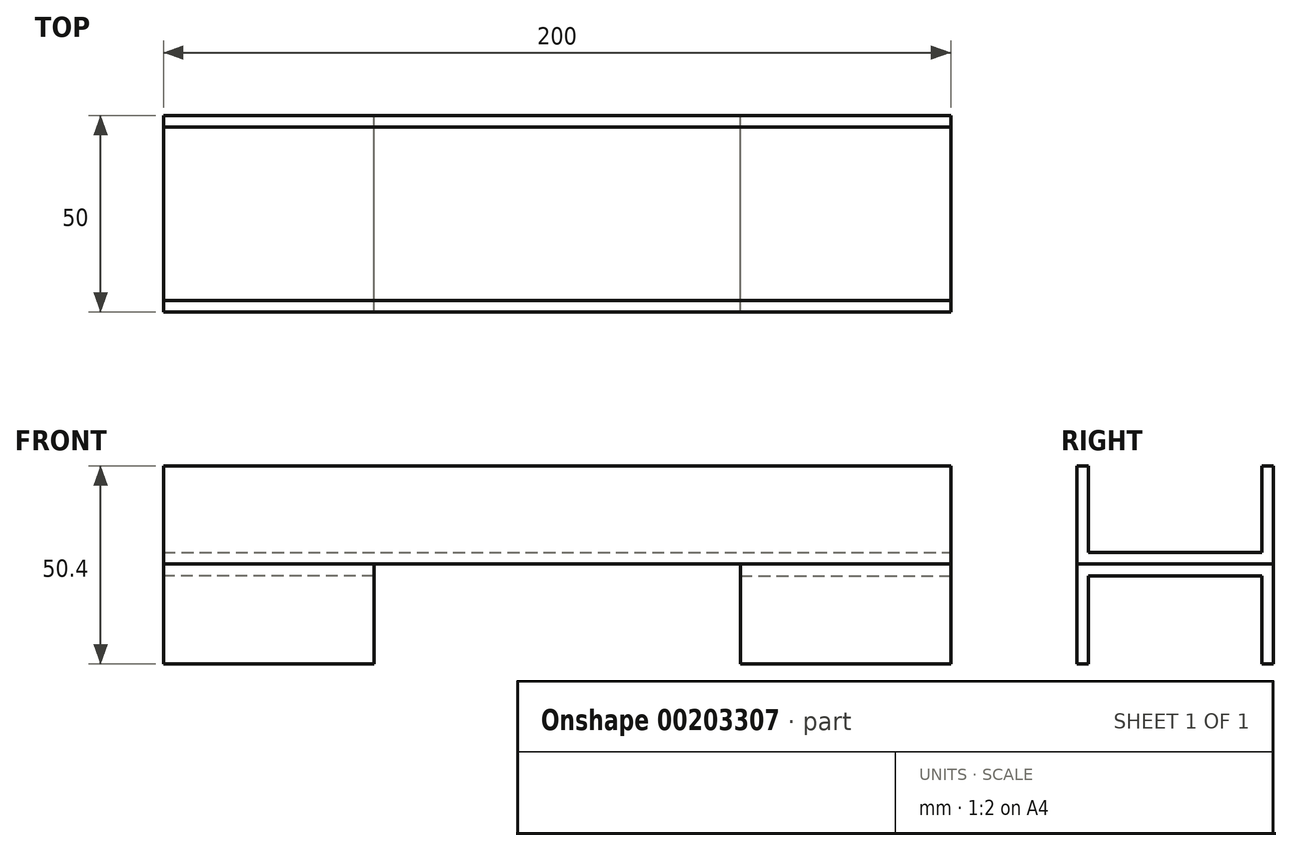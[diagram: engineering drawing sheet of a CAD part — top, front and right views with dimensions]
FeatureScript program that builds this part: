
annotation { "Feature Type Name" : "Feature", "Feature Type Description" : "" }
export const myFeature = defineFeature(function(context is Context, id is Id, definition is map)
    precondition{}
    {
        {
            var Q0;
            Q0=qCreatedBy(makeId("Front.planeOp"),FACE);
            var sketch = newSketch(context, id + "F0", { "sketchPlane" : qUnion([Q0])});
            skLineSegment(sketch, "E0.bottom", {"start": v(100, -12.5) * mm, "end": v(-100, -12.5) * mm});
            skLineSegment(sketch, "E0.top", {"start": v(100, 12.5) * mm, "end": v(-100, 12.5) * mm});
            skLineSegment(sketch, "E0.left", {"start": v(100, -12.5) * mm, "end": v(100, 12.5) * mm});
            skLineSegment(sketch, "E0.right", {"start": v(-100, -12.5) * mm, "end": v(-100, 12.5) * mm});
            skPoint(sketch, "E0.middle", {"position": v(0, 0) * mm});
            skSolve(sketch);
        }
        {
            var Q0;
            Q0 = qSketchRegion(id + "F0", true);
            var Q1;
            Q1 = qSketchRegion(id + "F2", true);
            extrude(context, id + "F1", {"entities" : qUnion([Q0, Q1]), "depth" : 50 * mm});
        }
        {
            var Q0;
            Q0=makeQuery(id+"F1.opExtrude","SWEPT_FACE",FACE,{"disambiguationData":[OSD([sQuery(id+"F0.wireOp",EDGE,"E0.left")])]});
            var sketch = newSketch(context, id + "F2", { "sketchPlane" : qUnion([Q0])});
            skLineSegment(sketch, "E1.bottom", {"start": v(-47, 12.5) * mm, "end": v(-3, 12.5) * mm});
            skLineSegment(sketch, "E1.top", {"start": v(-47, -9.5) * mm, "end": v(-3, -9.5) * mm});
            skLineSegment(sketch, "E1.left", {"start": v(-47, 12.5) * mm, "end": v(-47, -9.5) * mm});
            skLineSegment(sketch, "E1.right", {"start": v(-3, 12.5) * mm, "end": v(-3, -9.5) * mm});
            skLineSegment(sketch, "E2", {"start": v(-50, 0) * mm, "end": v(-47, 0) * mm, "construction": true});
            skPoint(sketch, "E2.endSnap0", {"position": v(-47, 1.5) * mm});
            skLineSegment(sketch, "E3", {"start": v(-9.09, -12.5) * mm, "end": v(-9.09, -9.5) * mm, "construction": true});
            skLineSegment(sketch, "E4", {"start": v(-3, 0) * mm, "end": v(0, 0) * mm, "construction": true});
            skSolve(sketch);
        }
        {
            var Q0;
            Q0 = qSketchRegion(id + "F2", true);
            extrude(context, id + "F3", {"entities" : qUnion([Q0]), "operationType" : NewBodyOperationType.REMOVE, "endBound" : BoundingType.THROUGH_ALL, "oppositeDirection" : true, "depth" : 25.4 * mm});
        }
        {
            var Q0;
            Q0=makeQuery(id+"F1.opExtrude","SWEPT_FACE",FACE,{"disambiguationData":[OSD([sQuery(id+"F0.wireOp",EDGE,"E0.bottom")])]});
            var sketch = newSketch(context, id + "F4", { "sketchPlane" : qUnion([Q0])});
            skLineSegment(sketch, "E5.bottom", {"start": v(-100, 50) * mm, "end": v(-46.54, 50) * mm});
            skLineSegment(sketch, "E5.top", {"start": v(-100, 0) * mm, "end": v(-46.54, 0) * mm});
            skLineSegment(sketch, "E5.left", {"start": v(-100, 50) * mm, "end": v(-100, 0) * mm});
            skLineSegment(sketch, "E5.right", {"start": v(-46.54, 50) * mm, "end": v(-46.54, 0) * mm});
            skSolve(sketch);
        }
        {
            var Q0;
            Q0 = qSketchRegion(id + "F4", true);
            extrude(context, id + "F5", {"entities" : qUnion([Q0]), "depth" : 25.4 * mm});
        }
        {
            var Q0;
            Q0=makeQuery(id+"F5.opExtrude","SWEPT_FACE",FACE,{"disambiguationData":[OSD([sQuery(id+"F4.wireOp",EDGE,"E5.left")])]});
            var sketch = newSketch(context, id + "F6", { "sketchPlane" : qUnion([Q0])});
            skLineSegment(sketch, "E6.bottom", {"start": v(3, -37.9) * mm, "end": v(47, -37.9) * mm});
            skLineSegment(sketch, "E6.top", {"start": v(3, -15.5) * mm, "end": v(47, -15.5) * mm});
            skLineSegment(sketch, "E6.left", {"start": v(3, -37.9) * mm, "end": v(3, -15.5) * mm});
            skLineSegment(sketch, "E6.right", {"start": v(47, -37.9) * mm, "end": v(47, -15.5) * mm});
            skLineSegment(sketch, "E7", {"start": v(25, -15.5) * mm, "end": v(25, -12.5) * mm, "construction": true});
            skLineSegment(sketch, "E8", {"start": v(3, -26.7) * mm, "end": v(0, -26.7) * mm, "construction": true});
            skLineSegment(sketch, "E9", {"start": v(47, -26.7) * mm, "end": v(50, -26.7) * mm, "construction": true});
            skSolve(sketch);
        }
        {
            var Q0;
            Q0=makeQuery(id+"F6.imprint","IMPRINT",FACE,{"disambiguationData":[TD([[makeQuery(id+"F6.imprint","IMPRINT",EDGE,{"derivedFrom":sQuery(id+"F6.wireOp",EDGE,"E6.bottom")}),-1.0]])]});
            extrude(context, id + "F7", {"entities" : qUnion([Q0]), "operationType" : NewBodyOperationType.REMOVE, "endBound" : BoundingType.THROUGH_ALL, "oppositeDirection" : true, "depth" : 25.4 * mm});
        }
        {
            var Q0;
            Q0=makeQuery(id+"F5.opExtrude","SWEPT_BODY",BODY,{"disambiguationData":[OSD([sQuery(id+"F4.wireOp",EDGE,"E5.bottom"),sQuery(id+"F4.wireOp",EDGE,"E5.top"),sQuery(id+"F4.wireOp",EDGE,"E5.left"),sQuery(id+"F4.wireOp",EDGE,"E5.right")])]});
            var Q1;
            Q1=qCreatedBy(makeId("Right.planeOp"),FACE);
            mirror(context, id + "F8", {"entities" : qUnion([Q0]), "mirrorPlane" : qUnion([Q1])});
        }
    });
